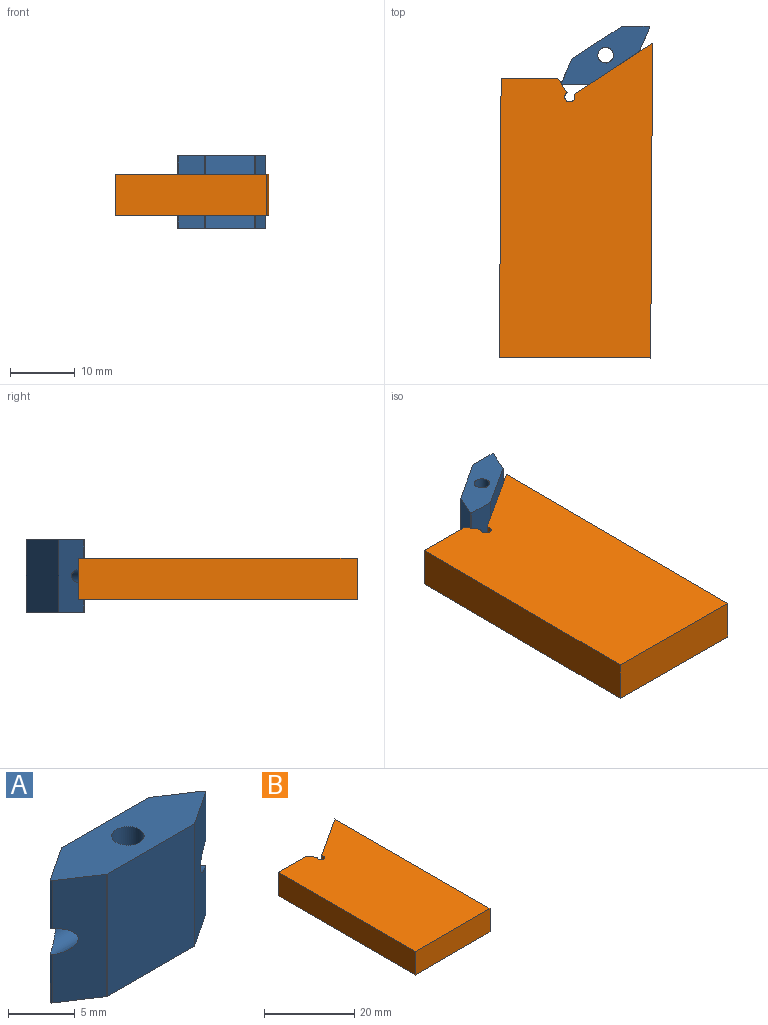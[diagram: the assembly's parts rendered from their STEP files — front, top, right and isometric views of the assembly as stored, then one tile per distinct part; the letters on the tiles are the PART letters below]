
ASSEMBLY  parts=2 mates=1
PART A: 19 faces, bbox 16.3x4.8x11.2 mm
  f0: plane 11.18x3.43mm, normal (-0.55,0.84,0), area 42.2mm2, adj f7,f8,f10,f11,f12,f18
  f1: plane 11.18x3.43mm, normal (-0.55,-0.84,0), area 42.2mm2, adj f7,f8,f10,f11,f12,f14
  f2: plane 11.18x9.2mm, normal (0,-1,0), area 102.8mm2, adj f7,f8,f14,f15
  f3: plane 11.18x3.43mm, normal (0.55,-0.84,0), area 42.2mm2, adj f7,f8,f9,f13,f15,f16
  f4: plane 11.18x3.43mm, normal (0.55,0.84,0), area 42.2mm2, adj f7,f8,f9,f13,f16,f17
  f5: plane 11.18x9.2mm, normal (0,1,0), area 102.8mm2, adj f7,f8,f17,f18
  f6: cylinder r=1.21mm len=11.18mm, axis (0,0,-1), area 73.6mm2, adj f7,f8,f9,f10
  f7: plane 16.3x4.76mm, normal (0,0,1), area 56.8mm2, adj f0,f1,f2,f3,f4,f5,f6,f12
  f8: plane 16.3x4.76mm, normal (0,0,-1), area 56.8mm2, adj f0,f1,f2,f3,f4,f5,f6,f11
  f9: cylinder r=1.19mm len=7.96mm, axis (1,0,0), area 47.2mm2, adj f3,f4,f6,f13,f16
  f10: cylinder r=1.19mm len=7.96mm, axis (1,0,0), area 47.2mm2, adj f0,f1,f6,f11,f12
  f11: cylinder r=0.13mm len=4.4mm, axis (0,0,-1), area 1.1mm2, adj f0,f1,f8,f10
  f12: cylinder r=0.13mm len=4.4mm, axis (0,0,-1), area 1.1mm2, adj f0,f1,f7,f10
  f13: cylinder r=0.13mm len=4.4mm, axis (0,0,-1), area 1.1mm2, adj f3,f4,f8,f9
  f14: cylinder r=0.13mm len=11.18mm, axis (0,0,-1), area 0.8mm2, adj f1,f2,f7,f8
  f15: cylinder r=0.13mm len=11.18mm, axis (0,0,-1), area 0.8mm2, adj f2,f3,f7,f8
  f16: cylinder r=0.13mm len=4.4mm, axis (0,0,-1), area 1.1mm2, adj f3,f4,f7,f9
  f17: cylinder r=0.13mm len=11.18mm, axis (0,0,-1), area 0.8mm2, adj f4,f5,f7,f8
  f18: cylinder r=0.13mm len=11.18mm, axis (0,0,-1), area 0.8mm2, adj f0,f5,f7,f8
PART B: 9 faces, bbox 23.4x48.7x6.4 mm
  f0: plane 43.15x6.35mm, normal (-1,0,0), area 274mm2, adj f1,f6,f7,f8
  f1: plane 23.4x6.35mm, normal (0,-1,0), area 148.6mm2, adj f0,f2,f7,f8
  f2: plane 48.72x6.35mm, normal (1,0,0), area 309.4mm2, adj f1,f3,f7,f8
  f3: plane 12.09x7.95mm, normal (-0.55,0.84,0), area 91.9mm2, adj f2,f4,f7,f8
  f4: cylinder r=0.79mm len=6.35mm, axis (0,0,-1), area 23.8mm2, adj f3,f5,f7,f8
  f5: plane 6.35x2.16mm, normal (0.84,0.55,0), area 16.4mm2, adj f4,f6,f7,f8
  f6: plane 8.79x6.35mm, normal (0,1,0), area 55.8mm2, adj f0,f5,f7,f8
  f7: plane 48.72x23.4mm, normal (0,0,1), area 1023.2mm2, adj f0,f1,f2,f3,f4,f5,f6
  f8: plane 48.72x23.4mm, normal (0,0,-1), area 1023.2mm2, adj f0,f1,f2,f3,f4,f5,f6
PLACE A rot(axis=(0,0,1),33deg) t=(-17.27,25.98,0.43)mm
PLACE B rot(axis=(0,0,-1),0.3deg) t=(-22.75,0.31,0)mm
MATE planar B.f3 <-> A.f2  axis (-0.54,0.84,0) through (-16.08,23.92,0)mm
